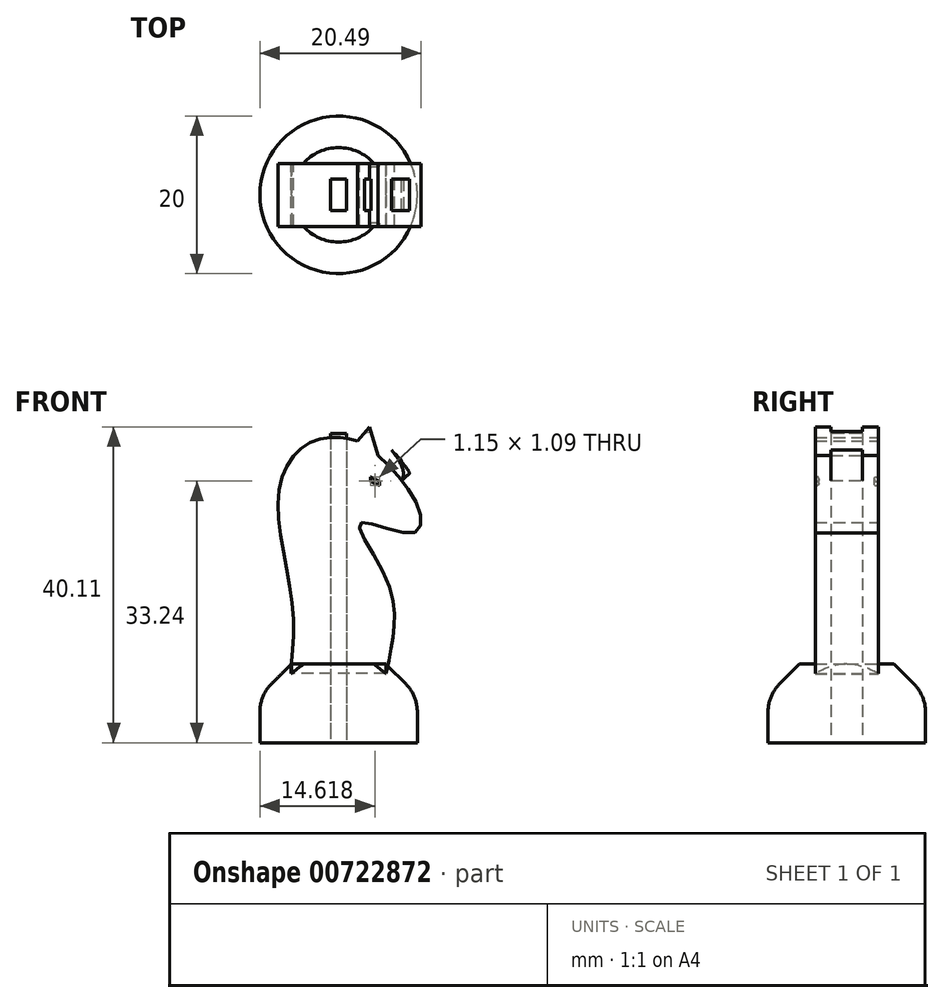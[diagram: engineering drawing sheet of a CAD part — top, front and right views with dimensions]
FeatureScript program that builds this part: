
annotation { "Feature Type Name" : "Feature", "Feature Type Description" : "" }
export const myFeature = defineFeature(function(context is Context, id is Id, definition is map)
    precondition{}
    {
        {
            var Q0;
            Q0=qCreatedBy(makeId("Top.planeOp"),FACE);
            var sketch = newSketch(context, id + "F0", { "sketchPlane" : qUnion([Q0])});
            skCircle(sketch, "E0", {"center": v(0, 0) * mm, "radius": 10 * mm});
            skSolve(sketch);
        }
        {
            var Q0;
            Q0 = qSketchRegion(id + "F0", true);
            extrude(context, id + "F1", {"entities" : qUnion([Q0]), "depth" : 10 * mm, "offsetDistance" : 25 * mm});
        }
        {
            var Q0;
            Q0=makeQuery(id+"F1.opExtrude","CAP_EDGE",EDGE,{"disambiguationData":[OSD([sQuery(id+"F0.wireOp",EDGE,"E0")])],"isStart":false});
            chamfer(context, id + "F2", {"entities" : qUnion([Q0]), "width" : 4 * mm, "tangentPropagation" : true});
        }
        {
            var Q0;
            {var subQ0=sQuery(id+"F0.wireOp",EDGE,"E0");Q0=makeQuery(id+"F2.opChamfer","BLEND_EDGE",EDGE,{"blendedFrom":[makeQuery(id+"F1.opExtrude","CAP_EDGE",EDGE,{"disambiguationData":[OSD([subQ0])],"isStart":false}),makeQuery(id+"F1.opExtrude","SWEPT_FACE",FACE,{"disambiguationData":[OSD([subQ0])]})],"blendedInto":[makeQuery(id+"F1.opExtrude","SWEPT_FACE",FACE,{"disambiguationData":[OSD([subQ0])]})]});}
            fillet(context, id + "F3", {"entities" : qUnion([Q0]), "radius" : 5 * mm, "tangentPropagation" : true, "allowEdgeOverflow" : false});
        }
        {
            var Q0;
            Q0=makeQuery(id+"F1.opExtrude","CAP_FACE",FACE,{"disambiguationData":[OSD([sQuery(id+"F0.wireOp",EDGE,"E0")])],"isStart":true});
            var sketch = newSketch(context, id + "F4", { "sketchPlane" : qUnion([Q0])});
            skLineSegment(sketch, "E1.bottom", {"start": v(6, 4) * mm, "end": v(-6, 4) * mm});
            skLineSegment(sketch, "E1.top", {"start": v(6, -4) * mm, "end": v(-6, -4) * mm});
            skLineSegment(sketch, "E1.left", {"start": v(6, 4) * mm, "end": v(6, -4) * mm});
            skLineSegment(sketch, "E1.right", {"start": v(-6, 4) * mm, "end": v(-6, -4) * mm});
            skPoint(sketch, "E1.middle", {"position": v(0, 0) * mm});
            skSolve(sketch);
        }
        {
            var Q0;
            Q0 = qSketchRegion(id + "F4", true);
            extrude(context, id + "F5", {"entities" : qUnion([Q0]), "operationType" : NewBodyOperationType.ADD, "oppositeDirection" : true, "depth" : 10 * mm, "offsetDistance" : 25 * mm});
        }
        {
            var Q0;
            {var subQ1=sQuery(id+"F4.wireOp",EDGE,"E1.left");var subQ2=sQuery(id+"F4.wireOp",EDGE,"E1.top");Q0=makeQuery(id+"F5.boolean.opBoolean","SPLIT",FACE,{"disambiguationData":[TD([makeQuery(id+"F5.opExtrude","SWEPT_FACE",FACE,{"disambiguationData":[OSD([subQ1])]})])],"derivedFrom":makeQuery(id+"F5.opExtrude","SWEPT_FACE",FACE,{"disambiguationData":[OSD([subQ2])]})});}
            var sketch = newSketch(context, id + "F6", { "sketchPlane" : qUnion([Q0])});
            skFitSpline(sketch, "E2", {"points": [v(-6, 8.79) * mm, v(-7, 14.3) * mm, v(-6, 21) * mm, v(-2.82, 27.9) * mm, v(-9.44, 26.68) * mm, v(-10.14, 29.89) * mm, v(-5.03, 36.5) * mm, v(-2.05, 38.46) * mm, v(3.49, 38.17) * mm, v(7.61, 31.82) * mm, v(5.77, 15.95) * mm, v(6.02, 8.79) * mm, v(5.89, 8.79) * mm], "startDerivative": vector(-18.82, 78.72) * mm, "endDerivative": vector(-12.52, 4.42) * mm});
            skLineSegment(sketch, "E3", {"start": v(-6, 8.79) * mm, "end": v(6.02, 8.79) * mm});
            skLineSegment(sketch, "E4", {"start": v(-5.03, 36.5) * mm, "end": v(-3.95, 40.1) * mm});
            skLineSegment(sketch, "E5", {"start": v(-3.95, 40.1) * mm, "end": v(-2.41, 38.34) * mm});
            skSolve(sketch);
        }
        {
            var Q0;
            Q0 = qSketchRegion(id + "F6", true);
            extrude(context, id + "F7", {"entities" : qUnion([Q0]), "oppositeDirection" : true, "depth" : 8 * mm, "offsetDistance" : 25 * mm});
        }
        {
            var Q0;
            Q0=makeQuery(id+"F7.opExtrude","CAP_FACE",FACE,{"disambiguationData":[OSD([sQuery(id+"F6.wireOp",EDGE,"E2"),sQuery(id+"F6.wireOp",EDGE,"E3")])],"isStart":true});
            var sketch = newSketch(context, id + "F8", { "sketchPlane" : qUnion([Q0])});
            skLineSegment(sketch, "E6", {"start": v(-5.2, 32.7) * mm, "end": v(-5.2, 33.2) * mm});
            skLineSegment(sketch, "E7", {"start": v(-5.2, 33.2) * mm, "end": v(-4.04, 33.79) * mm});
            skLineSegment(sketch, "E8", {"start": v(-4.04, 33.79) * mm, "end": v(-4.04, 33.2) * mm});
            skLineSegment(sketch, "E9", {"start": v(-4.04, 33.2) * mm, "end": v(-5.2, 32.7) * mm});
            skSolve(sketch);
        }
        {
            var Q0;
            Q0 = qSketchRegion(id + "F8", true);
            extrude(context, id + "F9", {"entities" : qUnion([Q0]), "operationType" : NewBodyOperationType.REMOVE, "oppositeDirection" : true, "depth" : 8 * mm, "offsetDistance" : 25 * mm});
        }
        {
            var Q0;
            Q0=makeQuery(id+"F9.boolean.opBoolean","COPY",FACE,{"derivedFrom":makeQuery(id+"F9.opExtrude","SWEPT_FACE",FACE,{"disambiguationData":[OSD([sQuery(id+"F8.wireOp",EDGE,"E9")])]})});
            var sketch = newSketch(context, id + "F10", { "sketchPlane" : qUnion([Q0])});
            skLineSegment(sketch, "E10.bottom", {"start": v(-8.53, 3.53) * mm, "end": v(-10.16, 3.53) * mm});
            skLineSegment(sketch, "E10.top", {"start": v(-8.53, -3.56) * mm, "end": v(-10.16, -3.56) * mm});
            skLineSegment(sketch, "E10.left", {"start": v(-8.53, 3.53) * mm, "end": v(-8.53, -3.56) * mm});
            skLineSegment(sketch, "E10.right", {"start": v(-10.16, 3.53) * mm, "end": v(-10.16, -3.56) * mm});
            skSolve(sketch);
        }
        {
            var Q0;
            Q0 = qSketchRegion(id + "F10", true);
            extrude(context, id + "F11", {"entities" : qUnion([Q0]), "operationType" : NewBodyOperationType.ADD, "depth" : 2 * mm, "offsetDistance" : 25 * mm});
        }
        {
            var Q0;
            Q0=makeQuery(id+"F11.boolean.opBoolean","INTERSECT",EDGE,{"derivedFrom":[makeQuery(id+"F9.boolean.opBoolean","COPY",FACE,{"derivedFrom":makeQuery(id+"F9.opExtrude","SWEPT_FACE",FACE,{"disambiguationData":[OSD([sQuery(id+"F8.wireOp",EDGE,"E7")])]})}),makeQuery(id+"F11.opExtrude","SWEPT_FACE",FACE,{"disambiguationData":[OSD([sQuery(id+"F10.wireOp",EDGE,"E10.top")])]})]});
            var Q1;
            Q1=makeQuery(id+"F11.boolean.opBoolean","INTERSECT",EDGE,{"derivedFrom":[makeQuery(id+"F9.boolean.opBoolean","COPY",FACE,{"derivedFrom":makeQuery(id+"F9.opExtrude","SWEPT_FACE",FACE,{"disambiguationData":[OSD([sQuery(id+"F8.wireOp",EDGE,"E8")])]})}),makeQuery(id+"F11.opExtrude","SWEPT_FACE",FACE,{"disambiguationData":[OSD([sQuery(id+"F10.wireOp",EDGE,"E10.top")])]})]});
            var Q2;
            Q2=makeQuery(id+"F11.opExtrude","CAP_EDGE",EDGE,{"disambiguationData":[OSD([sQuery(id+"F10.wireOp",EDGE,"E10.top")])],"isStart":true});
            var Q3;
            Q3=makeQuery(id+"F11.opExtrude","SWEPT_FACE",FACE,{"disambiguationData":[OSD([sQuery(id+"F10.wireOp",EDGE,"E10.top")])]});
            fillet(context, id + "F12", {"entities" : qUnion([Q0, Q1, Q2, Q3]), "radius" : 0.15 * mm, "tangentPropagation" : true, "allowEdgeOverflow" : false});
        }
        {
            var Q0;
            Q0=makeQuery(id+"F11.boolean.opBoolean","INTERSECT",EDGE,{"derivedFrom":[makeQuery(id+"F9.boolean.opBoolean","COPY",FACE,{"derivedFrom":makeQuery(id+"F9.opExtrude","SWEPT_FACE",FACE,{"disambiguationData":[OSD([sQuery(id+"F8.wireOp",EDGE,"E7")])]})}),makeQuery(id+"F11.opExtrude","SWEPT_FACE",FACE,{"disambiguationData":[OSD([sQuery(id+"F10.wireOp",EDGE,"E10.bottom")])]})]});
            var Q1;
            Q1=makeQuery(id+"F11.boolean.opBoolean","INTERSECT",EDGE,{"derivedFrom":[makeQuery(id+"F9.boolean.opBoolean","COPY",FACE,{"derivedFrom":makeQuery(id+"F9.opExtrude","SWEPT_FACE",FACE,{"disambiguationData":[OSD([sQuery(id+"F8.wireOp",EDGE,"E6")])]})}),makeQuery(id+"F11.opExtrude","SWEPT_FACE",FACE,{"disambiguationData":[OSD([sQuery(id+"F10.wireOp",EDGE,"E10.bottom")])]})]});
            var Q2;
            Q2=makeQuery(id+"F11.boolean.opBoolean","INTERSECT",EDGE,{"derivedFrom":[makeQuery(id+"F9.boolean.opBoolean","COPY",FACE,{"derivedFrom":makeQuery(id+"F9.opExtrude","SWEPT_FACE",FACE,{"disambiguationData":[OSD([sQuery(id+"F8.wireOp",EDGE,"E8")])]})}),makeQuery(id+"F11.opExtrude","SWEPT_FACE",FACE,{"disambiguationData":[OSD([sQuery(id+"F10.wireOp",EDGE,"E10.bottom")])]})]});
            var Q3;
            Q3=makeQuery(id+"F11.opExtrude","CAP_EDGE",EDGE,{"disambiguationData":[OSD([sQuery(id+"F10.wireOp",EDGE,"E10.bottom")])],"isStart":true});
            fillet(context, id + "F13", {"entities" : qUnion([Q0, Q1, Q2, Q3]), "radius" : 0.15 * mm, "tangentPropagation" : true, "allowEdgeOverflow" : false});
        }
        {
            var Q0;
            Q0=makeQuery(id+"F1.opExtrude","CAP_FACE",FACE,{"disambiguationData":[OSD([sQuery(id+"F0.wireOp",EDGE,"E0")])],"isStart":true});
            var sketch = newSketch(context, id + "F14", { "sketchPlane" : qUnion([Q0])});
            skLineSegment(sketch, "E11.bottom", {"start": v(1, -2) * mm, "end": v(-1, -2) * mm});
            skLineSegment(sketch, "E11.top", {"start": v(1, 2) * mm, "end": v(-1, 2) * mm});
            skLineSegment(sketch, "E11.left", {"start": v(1, -2) * mm, "end": v(1, 2) * mm});
            skLineSegment(sketch, "E11.right", {"start": v(-1, -2) * mm, "end": v(-1, 2) * mm});
            skPoint(sketch, "E11.middle", {"position": v(0, 0) * mm});
            skSolve(sketch);
        }
        {
            var Q0;
            Q0 = qSketchRegion(id + "F14", true);
            extrude(context, id + "F15", {"entities" : qUnion([Q0]), "oppositeDirection" : true, "depth" : 39.3 * mm, "offsetDistance" : 25 * mm});
        }
        {
            var Q0;
            Q0=makeQuery(id+"F15.opExtrude","SWEPT_FACE",FACE,{"disambiguationData":[OSD([sQuery(id+"F14.wireOp",EDGE,"E11.bottom")])]});
            var sketch = newSketch(context, id + "F16", { "sketchPlane" : qUnion([Q0])});
            skFitSpline(sketch, "E12", {"points": [v(-1, 38.68) * mm, v(-1.99, 36.53) * mm, v(-6.96, 33.17) * mm, v(-7.99, 33.34) * mm, v(-8.04, 35.07) * mm, v(-1.87, 40.77) * mm, v(5.88, 38.81) * mm, v(10.15, 29.91) * mm, v(9.6, 23.22) * mm, v(9.93, 19.6) * mm, v(4.86, 19.45) * mm, v(4.91, 19.45) * mm], "startDerivative": vector(-5.96, -28.6) * mm, "endDerivative": vector(8.93, -0.5) * mm});
            skFitSpline(sketch, "E13", {"points": [v(-7.99, 33.34) * mm, v(-8.9, 34.11) * mm, v(-9, 34.26) * mm, v(-6.72, 37.17) * mm], "startDerivative": vector(-3.49, 2.99) * mm, "endDerivative": vector(6.6, 6.51) * mm});
            skLineSegment(sketch, "E14", {"start": v(-1, 38.68) * mm, "end": v(4.88, 19.45) * mm});
            skSolve(sketch);
        }
        {
            var Q0;
            Q0 = qSketchRegion(id + "F16", true);
            extrude(context, id + "F17", {"entities" : qUnion([Q0]), "oppositeDirection" : true, "depth" : 4 * mm, "offsetDistance" : 25 * mm});
        }
        {
            var Q0;
            Q0=makeQuery(id+"F7.opExtrude","SWEPT_FACE",FACE,{"disambiguationData":[OSD([sQuery(id+"F6.wireOp",EDGE,"E4")])]});
            var sketch = newSketch(context, id + "F18", { "sketchPlane" : qUnion([Q0])});
            skLineSegment(sketch, "E15.bottom", {"start": v(-2, 36.73) * mm, "end": v(2, 36.73) * mm});
            skLineSegment(sketch, "E15.top", {"start": v(-2, 38.07) * mm, "end": v(2, 38.07) * mm});
            skLineSegment(sketch, "E15.left", {"start": v(-2, 36.73) * mm, "end": v(-2, 38.07) * mm});
            skLineSegment(sketch, "E15.right", {"start": v(2, 36.73) * mm, "end": v(2, 38.07) * mm});
            skSolve(sketch);
        }
        {
            var Q0;
            {var subQ0=sQuery(id+"F18.wireOp",EDGE,"E15.bottom");Q0=makeQuery(id+"F18.imprint","IMPRINT",FACE,{"disambiguationData":[TD([[makeQuery(id+"F18.imprint","IMPRINT",EDGE,{"derivedFrom":subQ0}),1.0]])]});}
            extrude(context, id + "F19", {"entities" : qUnion([Q0]), "operationType" : NewBodyOperationType.REMOVE, "oppositeDirection" : true, "depth" : 1 * mm, "offsetDistance" : 25 * mm});
        }
    });
